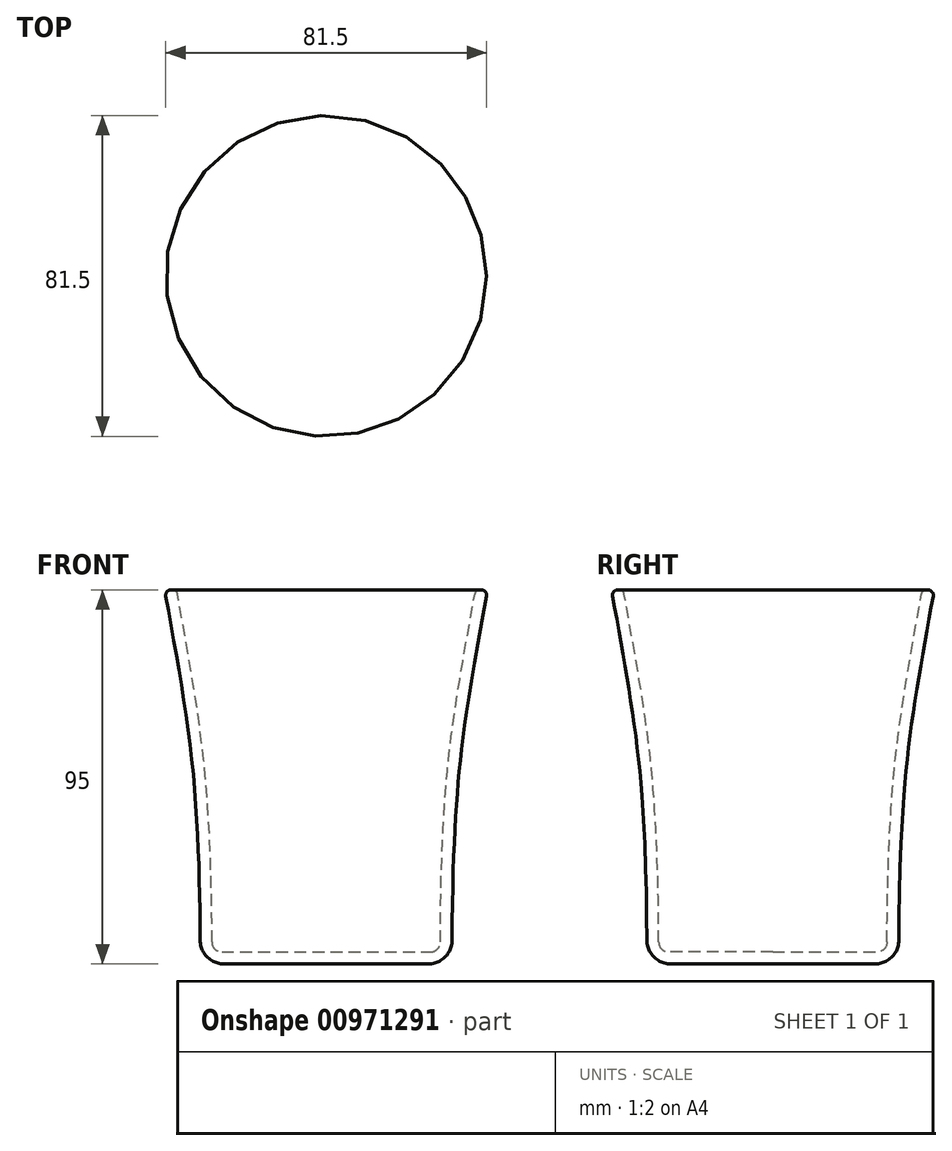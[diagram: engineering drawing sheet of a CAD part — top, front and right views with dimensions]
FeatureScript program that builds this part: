
annotation { "Feature Type Name" : "Feature", "Feature Type Description" : "" }
export const myFeature = defineFeature(function(context is Context, id is Id, definition is map)
    precondition{}
    {
        {
            var Q0;
            Q0=qCreatedBy(makeId("Front.planeOp"),FACE);
            var sketch = newSketch(context, id + "F0", { "sketchPlane" : qUnion([Q0])});
            skLineSegment(sketch, "E0", {"start": v(32, 0) * mm, "end": v(0, 0) * mm});
            skLineSegment(sketch, "E1", {"start": v(41, 95) * mm, "end": v(0, 95) * mm});
            skLineSegment(sketch, "E2", {"start": v(0, 95) * mm, "end": v(0, 0) * mm});
            skFitSpline(sketch, "E3", {"points": [v(32, 0) * mm, v(33.5, 45.37) * mm, v(41, 95) * mm], "startDerivative": vector(-0.22, 130.24) * mm, "endDerivative": vector(30.09, 166.02) * mm});
            skSolve(sketch);
        }
        {
            var Q0;
            Q0=makeQuery(id+"F0.imprint","IMPRINT",FACE,{"disambiguationData":[TD([[makeQuery(id+"F0.imprint","IMPRINT",EDGE,{"derivedFrom":sQuery(id+"F0.wireOp",EDGE,"a5036fc4-7fcf-42f1-8d1e-49c8a221e5f8")}),1.0]])]});
            var Q1;
            Q1=makeQuery(id+"F0.imprint","IMPRINT",FACE,{"disambiguationData":[TD([[makeQuery(id+"F0.imprint","IMPRINT",EDGE,{"derivedFrom":sQuery(id+"F0.wireOp",EDGE,"E0")}),-1.0]])]});
            var Q2;
            Q2=sQuery(id+"F0.wireOp",EDGE,"E2");
            revolve(context, id + "F1", {"surfaceOperationType" : NewSurfaceOperationType.NEW, "entities" : qUnion([Q0, Q1]), "axis" : qUnion([Q2]), "revolveType" : RevolveType.FULL});
        }
        {
            var Q0;
            Q0=makeQuery(id+"F1.opRevolve","SWEPT_FACE",FACE,{"disambiguationData":[OSD([sQuery(id+"F0.wireOp",EDGE,"E1")])]});
            shell(context, id + "F2", {"entities" : qUnion([Q0]), "thickness" : 3 * mm});
        }
        {
            var Q0;
            Q0=makeQuery(id+"F1.opRevolve","SWEPT_EDGE",EDGE,{"disambiguationData":[OSD([sQuery(id+"F0.wireOp",EDGE,"a5036fc4-7fcf-42f1-8d1e-49c8a221e5f8"),sQuery(id+"F0.wireOp",EDGE,"E0")])]});
            fillet(context, id + "F3", {"entities" : qUnion([Q0]), "radius" : 6 * mm, "tangentPropagation" : true, "allowEdgeOverflow" : false});
        }
        {
            var Q0;
            Q0=makeQuery(id+"F1.opRevolve","SWEPT_EDGE",EDGE,{"disambiguationData":[OSD([sQuery(id+"F0.wireOp",EDGE,"a5036fc4-7fcf-42f1-8d1e-49c8a221e5f8"),sQuery(id+"F0.wireOp",EDGE,"E1")])]});
            var Q1;
            Q1=makeQuery(id+"F2.opShell","OFFSET_EDGE",EDGE,{"disambiguationData":[OSD([sQuery(id+"F0.wireOp",EDGE,"a5036fc4-7fcf-42f1-8d1e-49c8a221e5f8"),sQuery(id+"F0.wireOp",EDGE,"E1")])]});
            fillet(context, id + "F4", {"entities" : qUnion([Q0, Q1]), "radius" : 1.27 * mm, "tangentPropagation" : true, "allowEdgeOverflow" : false});
        }
        {
            var Q0;
            Q0=makeQuery(id+"F2.opShell","OFFSET_EDGE",EDGE,{"disambiguationData":[OSD([sQuery(id+"F0.wireOp",EDGE,"a5036fc4-7fcf-42f1-8d1e-49c8a221e5f8"),sQuery(id+"F0.wireOp",EDGE,"E0")])]});
            fillet(context, id + "F5", {"entities" : qUnion([Q0]), "radius" : 2.54 * mm, "tangentPropagation" : true, "allowEdgeOverflow" : false});
        }
    });
